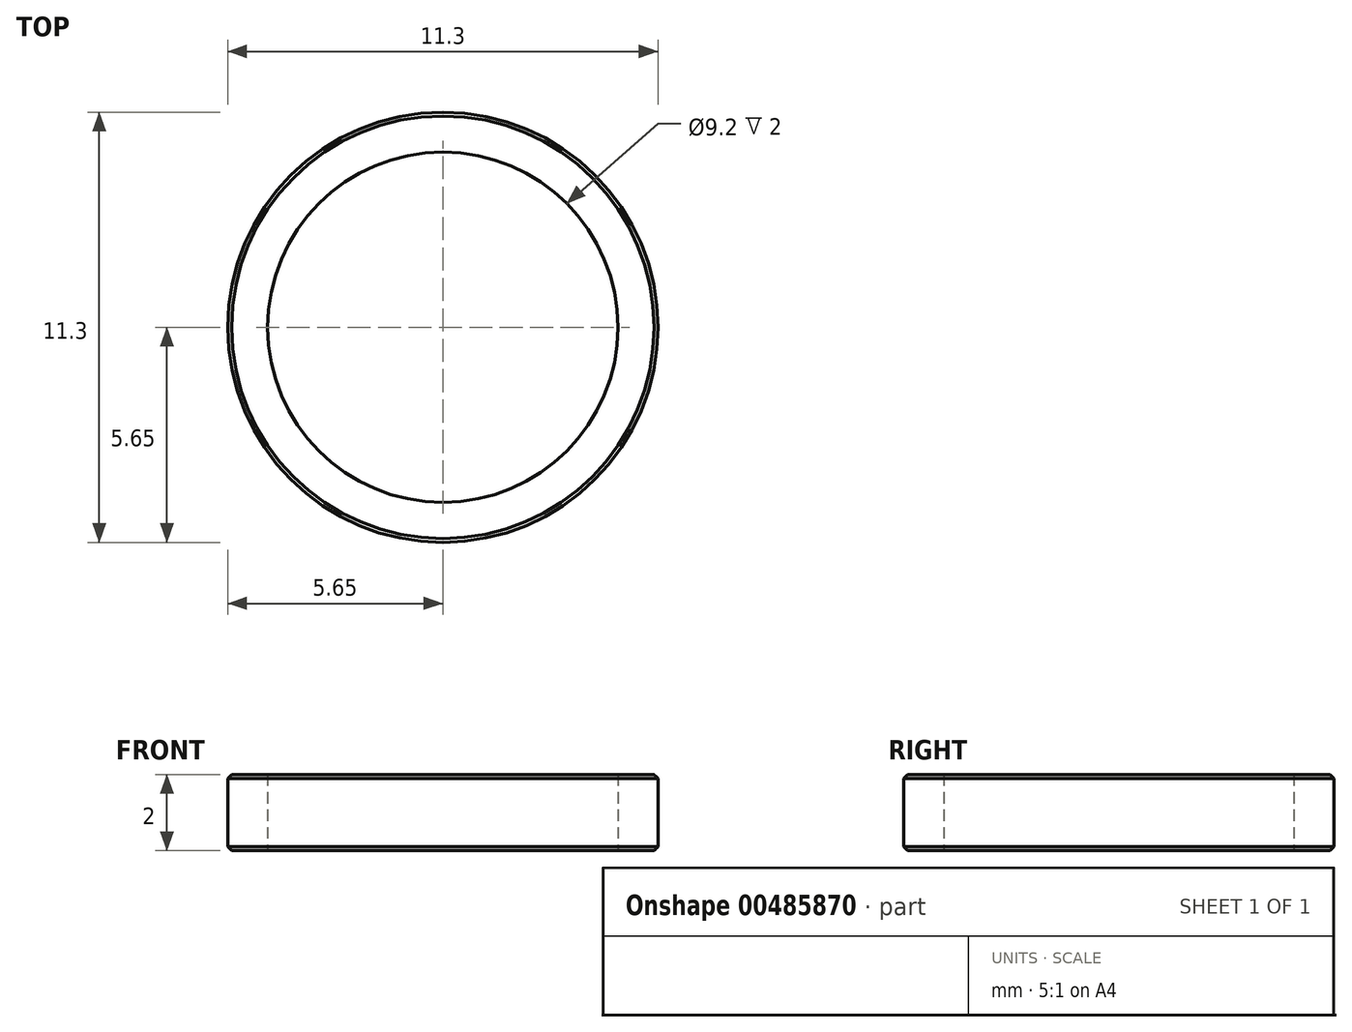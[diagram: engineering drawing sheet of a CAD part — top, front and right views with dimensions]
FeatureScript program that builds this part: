
annotation { "Feature Type Name" : "Feature", "Feature Type Description" : "" }
export const myFeature = defineFeature(function(context is Context, id is Id, definition is map)
    precondition{}
    {
        {
            var Q0;
            Q0=qCreatedBy(makeId("Top.planeOp"),FACE);
            var sketch = newSketch(context, id + "F0", { "sketchPlane" : qUnion([Q0])});
            skCircle(sketch, "E0", {"center": v(0, 0) * mm, "radius": 4.6 * mm});
            skCircle(sketch, "E1", {"center": v(0, 0) * mm, "radius": 5.65 * mm});
            skSolve(sketch);
        }
        {
            var Q0;
            Q0=makeQuery(id+"F0.imprint","IMPRINT",FACE,{"disambiguationData":[TD([[makeQuery(id+"F0.imprint","IMPRINT",EDGE,{"derivedFrom":sQuery(id+"F0.wireOp",EDGE,"E0")}),-1.0]])]});
            extrude(context, id + "F1", {"entities" : qUnion([Q0]), "depth" : 2 * mm, "offsetDistance" : 25 * mm});
        }
        {
            var Q0;
            Q0=makeQuery(id+"F1.opExtrude","CAP_EDGE",EDGE,{"disambiguationData":[OSD([sQuery(id+"F0.wireOp",EDGE,"E1")])],"isStart":false});
            var Q1;
            Q1=makeQuery(id+"F1.opExtrude","CAP_EDGE",EDGE,{"disambiguationData":[OSD([sQuery(id+"F0.wireOp",EDGE,"E1")])],"isStart":true});
            chamfer(context, id + "F2", {"entities" : qUnion([Q0, Q1]), "width" : 0.1 * mm, "tangentPropagation" : true});
        }
    });
